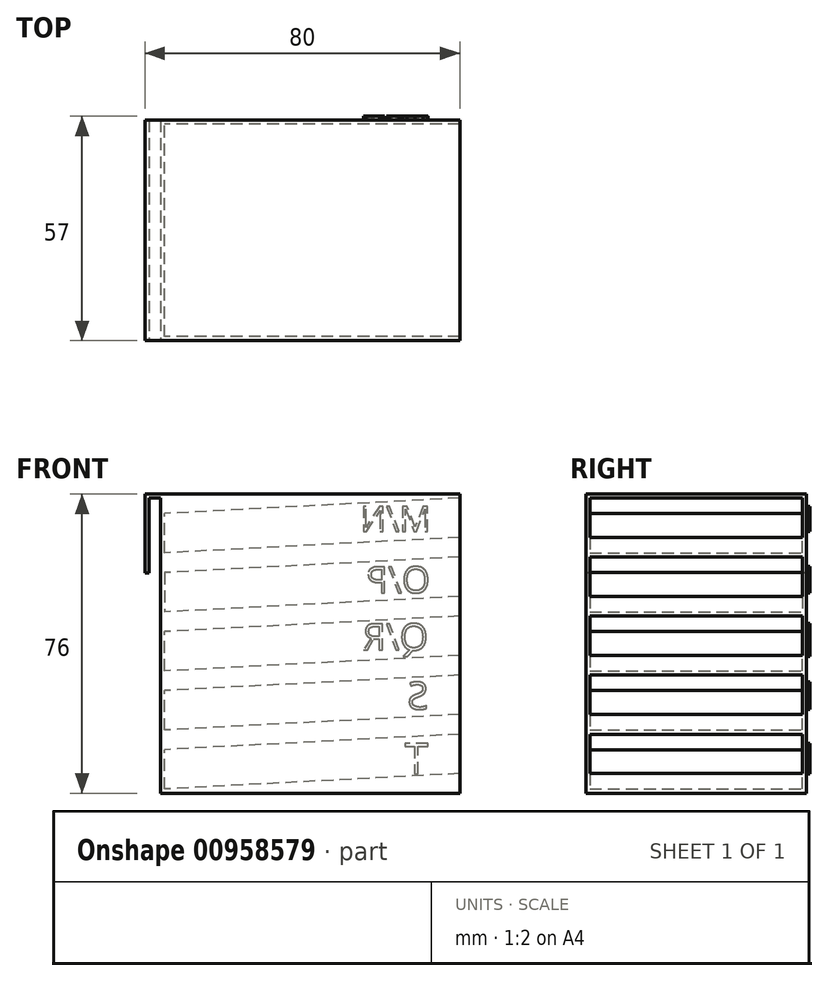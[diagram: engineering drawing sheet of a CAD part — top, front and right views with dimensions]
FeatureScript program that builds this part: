
annotation { "Feature Type Name" : "Feature", "Feature Type Description" : "" }
export const myFeature = defineFeature(function(context is Context, id is Id, definition is map)
    precondition{}
    {
        {
            var Q0;
            Q0=qCreatedBy(makeId("Front.planeOp"),FACE);
            var sketch = newSketch(context, id + "F0", { "sketchPlane" : qUnion([Q0])});
            skLineSegment(sketch, "E0.bottom", {"start": v(38, -38) * mm, "end": v(-38, -38) * mm});
            skLineSegment(sketch, "E0.top", {"start": v(38, 38) * mm, "end": v(-38, 38) * mm});
            skLineSegment(sketch, "E0.left", {"start": v(38, -38) * mm, "end": v(38, 38) * mm});
            skLineSegment(sketch, "E0.right", {"start": v(-38, -38) * mm, "end": v(-38, 38) * mm});
            skPoint(sketch, "E0.middle", {"position": v(0, 0) * mm});
            skSolve(sketch);
        }
        {
            var Q0;
            Q0=makeQuery(id+"F0.imprint","IMPRINT",FACE,{"disambiguationData":[TD([[makeQuery(id+"F0.imprint","IMPRINT",EDGE,{"derivedFrom":sQuery(id+"F0.wireOp",EDGE,"E0.bottom")}),-1.0]])]});
            extrude(context, id + "F1", {"entities" : qUnion([Q0]), "endBound" : BoundingType.SYMMETRIC, "oppositeDirection" : true, "depth" : 56 * mm, "offsetDistance" : 25 * mm});
        }
        {
            var Q0;
            Q0=makeQuery(id+"F1.opExtrude","SWEPT_FACE",FACE,{"disambiguationData":[OSD([sQuery(id+"F0.wireOp",EDGE,"E0.left")])]});
            var sketch = newSketch(context, id + "F2", { "sketchPlane" : qUnion([Q0])});
            skPoint(sketch, "E1", {"position": v(-28, 38) * mm});
            skPoint(sketch, "E2", {"position": v(-28, 37) * mm});
            skPoint(sketch, "E3", {"position": v(-27, 37) * mm});
            skLineSegment(sketch, "E4.bottom", {"start": v(-27, 37) * mm, "end": v(27, 37) * mm});
            skLineSegment(sketch, "E4.top", {"start": v(-27, 27) * mm, "end": v(27, 27) * mm});
            skLineSegment(sketch, "E4.left", {"start": v(-27, 37) * mm, "end": v(-27, 27) * mm});
            skLineSegment(sketch, "E4.right", {"start": v(27, 37) * mm, "end": v(27, 27) * mm});
            skPoint(sketch, "E5", {"position": v(-27, 27) * mm});
            skPoint(sketch, "E6", {"position": v(-27, 22) * mm});
            skLineSegment(sketch, "E7.bottom", {"start": v(-27, 22) * mm, "end": v(27, 22) * mm});
            skLineSegment(sketch, "E7.top", {"start": v(-27, 12) * mm, "end": v(27, 12) * mm});
            skLineSegment(sketch, "E7.left", {"start": v(-27, 22) * mm, "end": v(-27, 12) * mm});
            skLineSegment(sketch, "E7.right", {"start": v(27, 22) * mm, "end": v(27, 12) * mm});
            skPoint(sketch, "E8", {"position": v(-27, 7) * mm});
            skLineSegment(sketch, "E9.bottom", {"start": v(-27, 7) * mm, "end": v(27, 7) * mm});
            skLineSegment(sketch, "E9.top", {"start": v(-27, -3) * mm, "end": v(27, -3) * mm});
            skLineSegment(sketch, "E9.left", {"start": v(-27, 7) * mm, "end": v(-27, -3) * mm});
            skLineSegment(sketch, "E9.right", {"start": v(27, 7) * mm, "end": v(27, -3) * mm});
            skPoint(sketch, "E10", {"position": v(-27, -8) * mm});
            skLineSegment(sketch, "E11.bottom", {"start": v(-27, -8) * mm, "end": v(27, -8) * mm});
            skLineSegment(sketch, "E11.top", {"start": v(-27, -18) * mm, "end": v(27, -18) * mm});
            skLineSegment(sketch, "E11.left", {"start": v(-27, -8) * mm, "end": v(-27, -18) * mm});
            skLineSegment(sketch, "E11.right", {"start": v(27, -8) * mm, "end": v(27, -18) * mm});
            skPoint(sketch, "E12", {"position": v(-27, -23) * mm});
            skLineSegment(sketch, "E13.bottom", {"start": v(-27, -23) * mm, "end": v(27, -23) * mm});
            skLineSegment(sketch, "E13.top", {"start": v(-27, -33) * mm, "end": v(27, -33) * mm});
            skLineSegment(sketch, "E13.left", {"start": v(-27, -23) * mm, "end": v(-27, -33) * mm});
            skLineSegment(sketch, "E13.right", {"start": v(27, -23) * mm, "end": v(27, -33) * mm});
            skSolve(sketch);
        }
        {
            var Q0;
            Q0=makeQuery(id+"F1.opExtrude","CAP_FACE",FACE,{"disambiguationData":[OSD([sQuery(id+"F0.wireOp",EDGE,"E0.bottom"),sQuery(id+"F0.wireOp",EDGE,"E0.top"),sQuery(id+"F0.wireOp",EDGE,"E0.left"),sQuery(id+"F0.wireOp",EDGE,"E0.right")])],"isStart":true});
            var sketch = newSketch(context, id + "F3", { "sketchPlane" : qUnion([Q0])});
            skPoint(sketch, "E14", {"position": v(38, 22) * mm});
            skPoint(sketch, "E15", {"position": v(38, 7) * mm});
            skPoint(sketch, "E16", {"position": v(38, -8) * mm});
            skPoint(sketch, "E17", {"position": v(38, -23) * mm});
            skPoint(sketch, "E18", {"position": v(38, 37) * mm});
            skLineSegment(sketch, "E19", {"start": v(-38, 33.02) * mm, "end": v(-10.2, 33.02) * mm, "construction": true});
            skLineSegment(sketch, "E20", {"start": v(38, 37) * mm, "end": v(-38, 33.02) * mm});
            skLineSegment(sketch, "E21", {"start": v(38, 22) * mm, "end": v(-38, 18.02) * mm});
            skLineSegment(sketch, "E22", {"start": v(-38, 18.02) * mm, "end": v(-8.95, 18.02) * mm, "construction": true});
            skLineSegment(sketch, "E23", {"start": v(38, -23) * mm, "end": v(-38, -26.98) * mm});
            skLineSegment(sketch, "E24", {"start": v(-38, -26.98) * mm, "end": v(-9.06, -26.98) * mm, "construction": true});
            skLineSegment(sketch, "E25", {"start": v(38, 7) * mm, "end": v(-38, 3.02) * mm});
            skLineSegment(sketch, "E26", {"start": v(-38, 3.02) * mm, "end": v(-5.53, 3.02) * mm, "construction": true});
            skLineSegment(sketch, "E27", {"start": v(38, -8) * mm, "end": v(-38, -11.98) * mm});
            skLineSegment(sketch, "E28", {"start": v(-38, -11.98) * mm, "end": v(-6.01, -11.98) * mm});
            skSolve(sketch);
        }
        {
            var Q0;
            Q0=makeQuery(id+"F2.imprint","IMPRINT",FACE,{"disambiguationData":[TD([[makeQuery(id+"F2.imprint","IMPRINT",EDGE,{"derivedFrom":sQuery(id+"F2.wireOp",EDGE,"E4.bottom")}),-1.0]])]});
            var Q1;
            Q1=makeQuery(id+"F2.imprint","IMPRINT",FACE,{"disambiguationData":[TD([[makeQuery(id+"F2.imprint","IMPRINT",EDGE,{"derivedFrom":sQuery(id+"F2.wireOp",EDGE,"E7.bottom")}),-1.0]])]});
            var Q2;
            Q2=makeQuery(id+"F2.imprint","IMPRINT",FACE,{"disambiguationData":[TD([[makeQuery(id+"F2.imprint","IMPRINT",EDGE,{"derivedFrom":sQuery(id+"F2.wireOp",EDGE,"E9.bottom")}),-1.0]])]});
            var Q3;
            Q3=makeQuery(id+"F2.imprint","IMPRINT",FACE,{"disambiguationData":[TD([[makeQuery(id+"F2.imprint","IMPRINT",EDGE,{"derivedFrom":sQuery(id+"F2.wireOp",EDGE,"E11.bottom")}),-1.0]])]});
            var Q4;
            Q4=makeQuery(id+"F2.imprint","IMPRINT",FACE,{"disambiguationData":[TD([[makeQuery(id+"F2.imprint","IMPRINT",EDGE,{"derivedFrom":sQuery(id+"F2.wireOp",EDGE,"E13.bottom")}),-1.0]])]});
            var Q5;
            Q5=sQuery(id+"F3.wireOp",EDGE,"E20");
            sweep(context, id + "F4", {"operationType" : NewBodyOperationType.REMOVE, "profiles" : qUnion([Q0, Q1, Q2, Q3, Q4]), "path" : qUnion([Q5])});
        }
        {
            var Q0;
            Q0=makeQuery(id+"F1.opExtrude","SWEPT_FACE",FACE,{"disambiguationData":[OSD([sQuery(id+"F0.wireOp",EDGE,"E0.right")])]});
            var sketch = newSketch(context, id + "F5", { "sketchPlane" : qUnion([Q0])});
            skLineSegment(sketch, "E29.bottom", {"start": v(-28, 38) * mm, "end": v(28, 38) * mm});
            skLineSegment(sketch, "E29.top", {"start": v(-28, -38) * mm, "end": v(28, -38) * mm});
            skLineSegment(sketch, "E29.left", {"start": v(-28, 38) * mm, "end": v(-28, -38) * mm});
            skLineSegment(sketch, "E29.right", {"start": v(28, 38) * mm, "end": v(28, -38) * mm});
            skSolve(sketch);
        }
        {
            var Q0;
            Q0=qSketchRegion(id+"F5",true);
            extrude(context, id + "F6", {"entities" : qUnion([Q0]), "operationType" : NewBodyOperationType.ADD, "oppositeDirection" : true, "depth" : 1 * mm, "offsetDistance" : 25 * mm});
        }
        {
            var Q0;
            Q0=makeQuery(id+"F1.opExtrude","CAP_FACE",FACE,{"disambiguationData":[OSD([sQuery(id+"F0.wireOp",EDGE,"E0.bottom"),sQuery(id+"F0.wireOp",EDGE,"E0.top"),sQuery(id+"F0.wireOp",EDGE,"E0.left"),sQuery(id+"F0.wireOp",EDGE,"E0.right")])],"isStart":true});
            var sketch = newSketch(context, id + "F7", { "sketchPlane" : qUnion([Q0])});
            skLineSegment(sketch, "E30", {"start": v(-38, 38) * mm, "end": v(-42, 38) * mm});
            skLineSegment(sketch, "E31", {"start": v(-42, 38) * mm, "end": v(-42, 18) * mm});
            skLineSegment(sketch, "E32", {"start": v(-42, 18) * mm, "end": v(-41, 18) * mm});
            skLineSegment(sketch, "E33", {"start": v(-41, 18) * mm, "end": v(-41, 37) * mm});
            skLineSegment(sketch, "E34", {"start": v(-41, 37) * mm, "end": v(-38, 37) * mm});
            skSolve(sketch);
        }
        {
            var Q0;
            {var subQ0=sQuery(id+"F7.wireOp",EDGE,"E30");Q0=makeQuery(id+"F7.imprint","IMPRINT",FACE,{"disambiguationData":[TD([[makeQuery(id+"F7.imprint","IMPRINT",EDGE,{"derivedFrom":subQ0}),1.0]])]});}
            extrude(context, id + "F8", {"entities" : qUnion([Q0]), "operationType" : NewBodyOperationType.ADD, "oppositeDirection" : true, "depth" : 56 * mm, "offsetDistance" : 25 * mm});
        }
        {
            var Q0;
            {var subQ0=sQuery(id+"F0.wireOp",EDGE,"E0.right");Q0=makeQuery(id+"F8.boolean.opBoolean","MERGE",FACE,{"derivedFrom":[makeQuery(id+"F1.opExtrude","CAP_FACE",FACE,{"disambiguationData":[OSD([sQuery(id+"F0.wireOp",EDGE,"E0.bottom"),sQuery(id+"F0.wireOp",EDGE,"E0.top"),sQuery(id+"F0.wireOp",EDGE,"E0.left"),subQ0])],"isStart":false}),makeQuery(id+"F8.opExtrude","CAP_FACE",FACE,{"disambiguationData":[OSD([subQ0,sQuery(id+"F7.wireOp",EDGE,"E30"),sQuery(id+"F7.wireOp",EDGE,"E31"),sQuery(id+"F7.wireOp",EDGE,"E32"),sQuery(id+"F7.wireOp",EDGE,"E33"),sQuery(id+"F7.wireOp",EDGE,"E34")])],"isStart":false})]});}
            var sketch = newSketch(context, id + "F9", { "sketchPlane" : qUnion([Q0])});
            skText(sketch, "E35", { "text": "M/N", "fontName": "OpenSans-Regular.ttf"});
            skText(sketch, "E36", { "text": "O/P", "fontName": "OpenSans-Regular.ttf"});
            skText(sketch, "E37", { "text": "Q/R", "fontName": "OpenSans-Regular.ttf"});
            skText(sketch, "E38", { "text": "S", "fontName": "OpenSans-Regular.ttf"});
            skText(sketch, "E39", { "text": "T", "fontName": "OpenSans-Regular.ttf"});
            const initialGuessF9  = {"E35": [-0.03067, 0.02852, 1, 0, 0.00643], "E36": [-0.03044, 0.01292, 1, 0, 0.00667], "E37": [-0.02997, -0.00164, 1, 0, 0.00676], "E38": [-0.02997, -0.01666, 1, 0, 0.00695], "E39": [-0.02997, -0.03303, 1, 0, 0.0078]};
            skSetInitialGuess(sketch, initialGuessF9);
            skSolve(sketch);
        }
        {
            var Q0;
            Q0=qSketchRegion(id+"F9",true);
            extrude(context, id + "F10", {"entities" : qUnion([Q0]), "operationType" : NewBodyOperationType.ADD, "depth" : 1 * mm, "offsetDistance" : 25 * mm});
        }
    });
